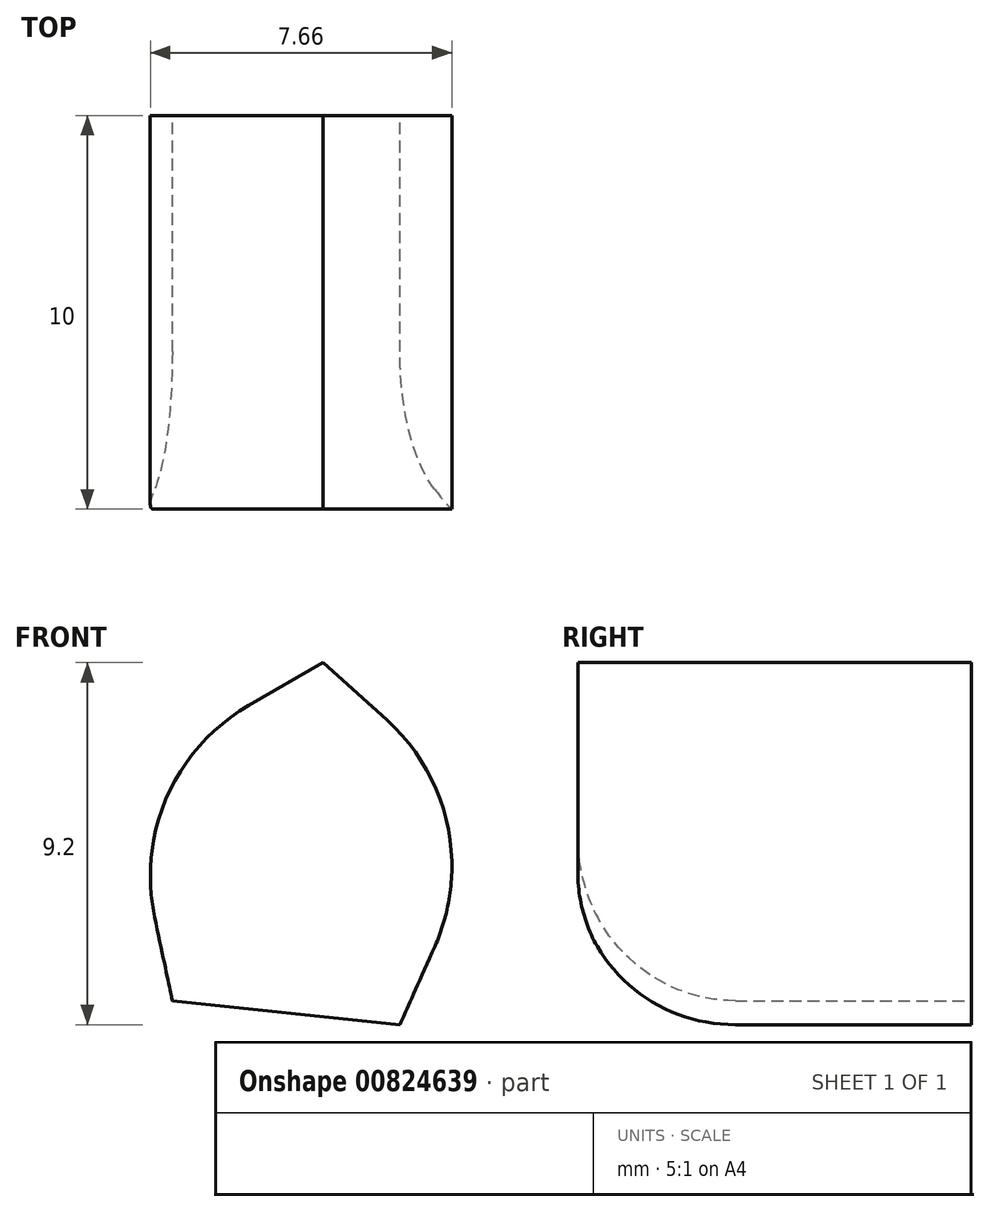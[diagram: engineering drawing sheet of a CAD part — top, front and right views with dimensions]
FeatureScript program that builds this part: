
annotation { "Feature Type Name" : "Feature", "Feature Type Description" : "" }
export const myFeature = defineFeature(function(context is Context, id is Id, definition is map)
    precondition{}
    {
        {
            var Q0;
            Q0=qCreatedBy(makeId("Front.planeOp"),FACE);
            var sketch = newSketch(context, id + "F0", { "sketchPlane" : qUnion([Q0])});
            skCircle(sketch, "E0.cCircle", {"center": v(0, 0) * mm, "radius": 4 * mm, "construction": true});
            skLineSegment(sketch, "E0.0", {"start": v(0.52, 4.92) * mm, "end": v(4.84, 1.03) * mm});
            skLineSegment(sketch, "E0.1", {"start": v(4.84, 1.03) * mm, "end": v(2.47, -4.28) * mm});
            skLineSegment(sketch, "E0.2", {"start": v(2.47, -4.28) * mm, "end": v(-3.31, -3.67) * mm});
            skLineSegment(sketch, "E0.3", {"start": v(-3.31, -3.67) * mm, "end": v(-4.52, 2.01) * mm});
            skLineSegment(sketch, "E0.4", {"start": v(-4.52, 2.01) * mm, "end": v(0.52, 4.92) * mm});
            skPoint(sketch, "E0.0.midPoint", {"position": v(2.68, 2.97) * mm});
            skSolve(sketch);
        }
        {
            var Q0;
            Q0=makeQuery(id+"F0.imprint","IMPRINT",FACE,{"disambiguationData":[TD([[makeQuery(id+"F0.imprint","IMPRINT",EDGE,{"derivedFrom":sQuery(id+"F0.wireOp",EDGE,"E0.0")}),-1.0]])]});
            extrude(context, id + "F1", {"entities" : qUnion([Q0]), "depth" : 10 * mm, "offsetDistance" : 25 * mm});
        }
        {
            var Q0;
            Q0=makeQuery(id+"F1.opExtrude","CAP_EDGE",EDGE,{"disambiguationData":[OSD([sQuery(id+"F0.wireOp",EDGE,"E0.2")])],"isStart":false});
            fillet(context, id + "F2", {"entities" : qUnion([Q0]), "radius" : 4 * mm, "tangentPropagation" : true, "allowEdgeOverflow" : false});
        }
        {
            var Q0;
            Q0=makeQuery(id+"F1.opExtrude","SWEPT_EDGE",EDGE,{"disambiguationData":[OSD([sQuery(id+"F0.wireOp",EDGE,"E0.0"),sQuery(id+"F0.wireOp",EDGE,"E0.1")])]});
            fillet(context, id + "F3", {"entities" : qUnion([Q0]), "radius" : 5 * mm, "tangentPropagation" : true, "allowEdgeOverflow" : false});
        }
        {
            var Q0;
            Q0=makeQuery(id+"F1.opExtrude","SWEPT_EDGE",EDGE,{"disambiguationData":[OSD([sQuery(id+"F0.wireOp",EDGE,"E0.3"),sQuery(id+"F0.wireOp",EDGE,"E0.4")])]});
            fillet(context, id + "F4", {"entities" : qUnion([Q0]), "radius" : 5 * mm, "tangentPropagation" : true, "allowEdgeOverflow" : false});
        }
    });
